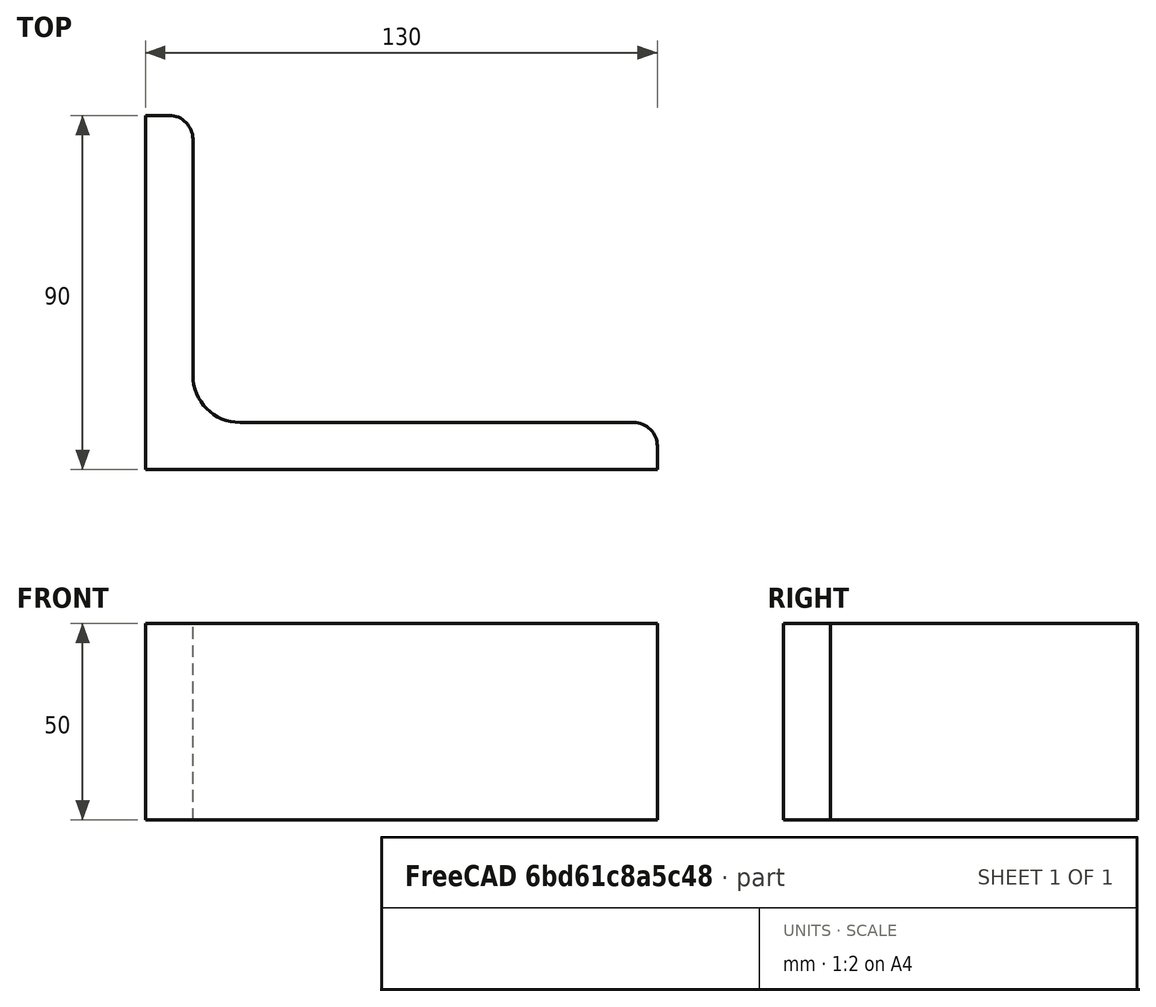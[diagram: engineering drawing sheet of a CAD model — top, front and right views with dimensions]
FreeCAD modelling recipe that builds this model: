
FCSTD DOCUMENT  (FreeCAD 0.15R4671 (Git))
Label: Angle Bar 130x90x12 EN10056 S235JR
License: All rights reserved
LicenseURL: http://en.wikipedia.org/wiki/All_rights_reserved
objects: Sketcher::SketchObject×1, Part::Extrusion×1
note: 2 computed .brp shape members not serialized (recipe doc carries the construction recipe); baked Part::Feature solids carry a one-line shape summary decoded from their .brp

FEATURE [Sketcher::SketchObject] Sketch
  sketch-geometry (9):
    g0: LineSegment StartX=0 StartY=0 StartZ=0 EndX=130 EndY=0 EndZ=0
    g1: LineSegment StartX=130 StartY=0 StartZ=0 EndX=130 EndY=6 EndZ=0
    g2: LineSegment StartX=124 StartY=12 StartZ=0 EndX=24 EndY=12 EndZ=0
    g3: LineSegment StartX=0 StartY=0 StartZ=0 EndX=0 EndY=90 EndZ=0
    g4: LineSegment StartX=0 StartY=90 StartZ=0 EndX=6 EndY=90 EndZ=0
    g5: LineSegment StartX=12 StartY=84 StartZ=0 EndX=12 EndY=24 EndZ=0
    g6: ArcOfCircle CenterX=24 CenterY=24 CenterZ=0 NormalX=0 NormalY=0 NormalZ=1 Radius=12 StartAngle=3.14159 EndAngle=4.71239
    g7: ArcOfCircle CenterX=6 CenterY=84 CenterZ=0 NormalX=0 NormalY=0 NormalZ=1 Radius=6 StartAngle=0 EndAngle=1.5708
    g8: ArcOfCircle CenterX=124 CenterY=6 CenterZ=0 NormalX=0 NormalY=0 NormalZ=1 Radius=6 StartAngle=0 EndAngle=1.5708
  constraints (23):
    c: Coincident(g0,g-1)
    c: Horizontal(g0)
    c: Coincident(g1,g0)
    c: Vertical(g1)
    c: Horizontal(g2)
    c: Coincident(g3,g-1)
    c: Vertical(g3)
    c: Coincident(g4,g3)
    c: Horizontal(g4)
    c: Vertical(g5)
    c: Tangent(g5,g6) = -1.5708
    c: Tangent(g2,g6) = 1.5708
    c: Tangent(g4,g7) = 1.5708
    c: Tangent(g5,g7) = 1.5708
    c: Tangent(g2,g8) = -1.5708
    c: Tangent(g1,g8) = -1.5708
    c: DistanceX(g0) = 130
    c: DistanceY(g3) = 90
    c: DistanceY(g0,g2) = 12
    c: DistanceX(g3,g5) = 12
    c: Radius(g6) = 12
    c: Radius(g8) = 6
    c: Radius(g7) = 6
FEATURE [Part::Extrusion] Extrude  label="Angle Bar 130x90x12 EN10056 S235JR"
  Base = -> Sketch
  Dir = (0,0,50)
  Solid = true
